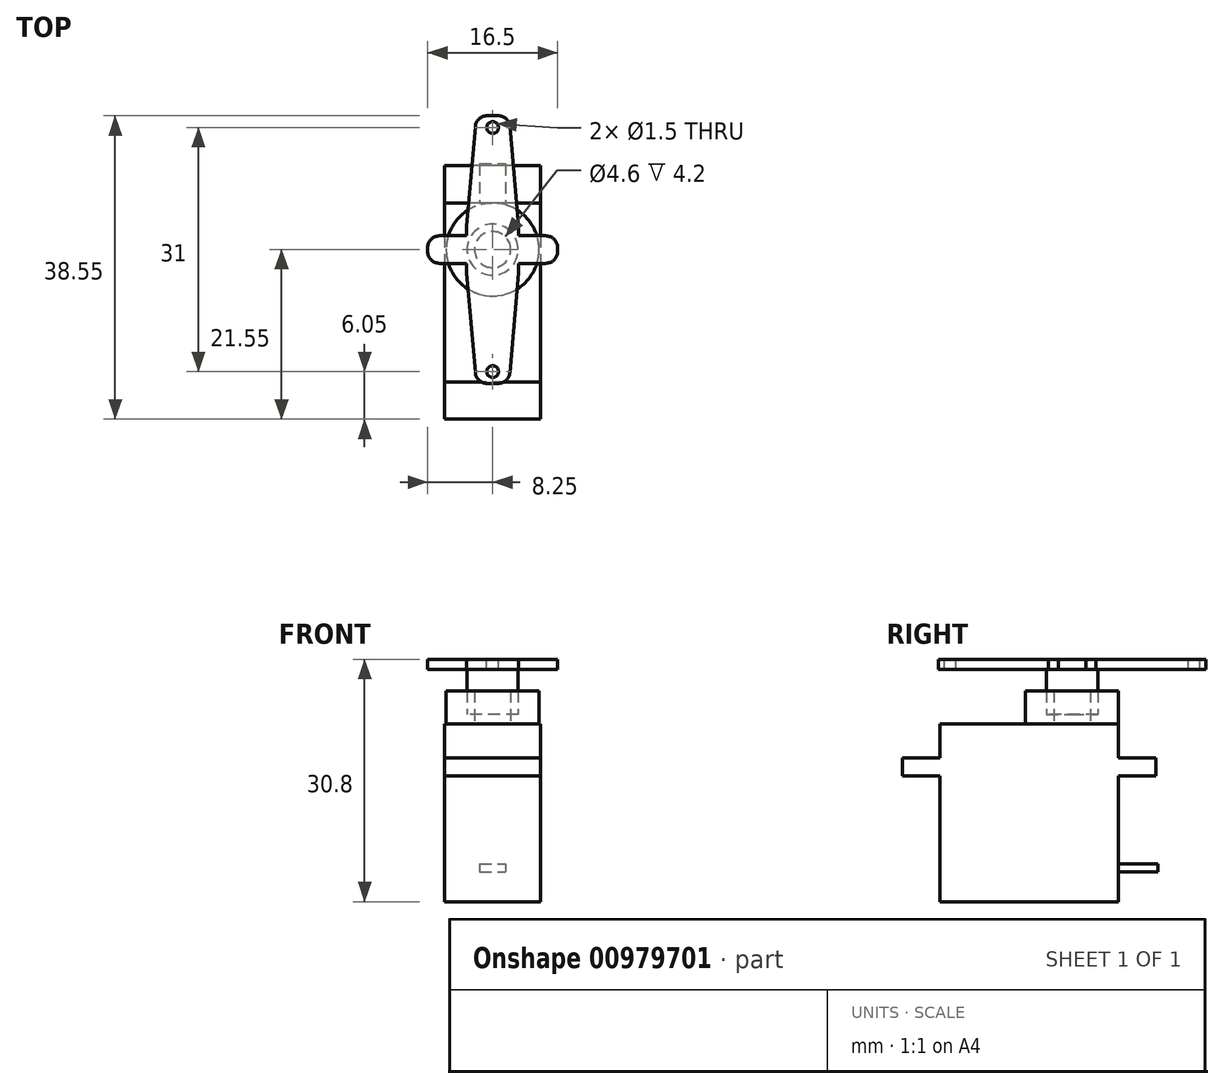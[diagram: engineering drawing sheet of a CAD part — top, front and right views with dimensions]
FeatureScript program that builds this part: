
annotation { "Feature Type Name" : "Feature", "Feature Type Description" : "" }
export const myFeature = defineFeature(function(context is Context, id is Id, definition is map)
    precondition{}
    {
        {
            var Q0;
            Q0=qCreatedBy(makeId("Top.planeOp"),FACE);
            var sketch = newSketch(context, id + "F0", { "sketchPlane" : qUnion([Q0])});
            skLineSegment(sketch, "E0.bottom", {"start": v(6.1, 11.35) * mm, "end": v(-6.1, 11.35) * mm});
            skLineSegment(sketch, "E0.top", {"start": v(6.1, -11.35) * mm, "end": v(-6.1, -11.35) * mm});
            skLineSegment(sketch, "E0.left", {"start": v(6.1, 11.35) * mm, "end": v(6.1, -11.35) * mm});
            skLineSegment(sketch, "E0.right", {"start": v(-6.1, 11.35) * mm, "end": v(-6.1, -11.35) * mm});
            skPoint(sketch, "E0.middle", {"position": v(0, 0) * mm});
            skSolve(sketch);
        }
        {
            var Q0;
            Q0=makeQuery(id+"F0.imprint","IMPRINT",FACE,{"disambiguationData":[TD([[makeQuery(id+"F0.imprint","IMPRINT",EDGE,{"derivedFrom":sQuery(id+"F0.wireOp",EDGE,"E0.bottom")}),1.0]])]});
            extrude(context, id + "F1", {"entities" : qUnion([Q0]), "depth" : 16 * mm, "offsetDistance" : 25 * mm});
        }
        {
            var Q0;
            Q0=makeQuery(id+"F1.opExtrude","CAP_FACE",FACE,{"disambiguationData":[OSD([sQuery(id+"F0.wireOp",EDGE,"E0.bottom"),sQuery(id+"F0.wireOp",EDGE,"E0.top"),sQuery(id+"F0.wireOp",EDGE,"E0.left"),sQuery(id+"F0.wireOp",EDGE,"E0.right")])],"isStart":false});
            var sketch = newSketch(context, id + "F2", { "sketchPlane" : qUnion([Q0])});
            skLineSegment(sketch, "E1.bottom", {"start": v(6.1, 16.1) * mm, "end": v(-6.1, 16.1) * mm});
            skLineSegment(sketch, "E1.top", {"start": v(6.1, -16.1) * mm, "end": v(-6.1, -16.1) * mm});
            skLineSegment(sketch, "E1.left", {"start": v(6.1, 16.1) * mm, "end": v(6.1, -16.1) * mm});
            skLineSegment(sketch, "E1.right", {"start": v(-6.1, 16.1) * mm, "end": v(-6.1, -16.1) * mm});
            skPoint(sketch, "E1.middle", {"position": v(0, 0) * mm});
            skSolve(sketch);
        }
        {
            var Q0;
            Q0 = qSketchRegion(id + "F2", true);
            extrude(context, id + "F3", {"entities" : qUnion([Q0]), "operationType" : NewBodyOperationType.ADD, "depth" : 2.3 * mm, "offsetDistance" : 25 * mm});
        }
        {
            var Q0;
            Q0=makeQuery(id+"F3.opExtrude","CAP_FACE",FACE,{"disambiguationData":[OSD([sQuery(id+"F2.wireOp",EDGE,"E1.bottom"),sQuery(id+"F2.wireOp",EDGE,"E1.top"),sQuery(id+"F2.wireOp",EDGE,"E1.left"),sQuery(id+"F2.wireOp",EDGE,"E1.right")])],"isStart":false});
            var sketch = newSketch(context, id + "F4", { "sketchPlane" : qUnion([Q0])});
            skLineSegment(sketch, "E2.bottom", {"start": v(6.1, 11.35) * mm, "end": v(-6.1, 11.35) * mm});
            skLineSegment(sketch, "E2.top", {"start": v(6.1, -11.35) * mm, "end": v(-6.1, -11.35) * mm});
            skLineSegment(sketch, "E2.left", {"start": v(6.1, 11.35) * mm, "end": v(6.1, -11.35) * mm});
            skLineSegment(sketch, "E2.right", {"start": v(-6.1, 11.35) * mm, "end": v(-6.1, -11.35) * mm});
            skPoint(sketch, "E2.middle", {"position": v(0, 0) * mm});
            skSolve(sketch);
        }
        {
            var Q0;
            Q0 = qSketchRegion(id + "F4", true);
            extrude(context, id + "F5", {"entities" : qUnion([Q0]), "operationType" : NewBodyOperationType.ADD, "depth" : 4.3 * mm, "offsetDistance" : 25 * mm});
        }
        {
            var Q0;
            Q0=makeQuery(id+"F5.opExtrude","CAP_FACE",FACE,{"disambiguationData":[OSD([sQuery(id+"F4.wireOp",EDGE,"E2.bottom"),sQuery(id+"F4.wireOp",EDGE,"E2.top"),sQuery(id+"F4.wireOp",EDGE,"E2.left"),sQuery(id+"F4.wireOp",EDGE,"E2.right")])],"isStart":false});
            var sketch = newSketch(context, id + "F6", { "sketchPlane" : qUnion([Q0])});
            skCircle(sketch, "E3", {"center": v(0, 5.45) * mm, "radius": 5.9 * mm});
            skCircle(sketch, "E4", {"center": v(0, 5.45) * mm, "radius": 2.3 * mm});
            skSolve(sketch);
        }
        {
            var Q0;
            Q0 = qSketchRegion(id + "F6", true);
            extrude(context, id + "F7", {"entities" : qUnion([Q0]), "operationType" : NewBodyOperationType.ADD, "depth" : 4.2 * mm, "offsetDistance" : 25 * mm});
        }
        {
            var Q0;
            Q0=makeQuery(id+"F1.opExtrude","SWEPT_FACE",FACE,{"disambiguationData":[OSD([sQuery(id+"F0.wireOp",EDGE,"E0.bottom")])]});
            var sketch = newSketch(context, id + "F8", { "sketchPlane" : qUnion([Q0])});
            skLineSegment(sketch, "E5.bottom", {"start": v(1.65, 4.8) * mm, "end": v(-1.65, 4.8) * mm});
            skLineSegment(sketch, "E5.top", {"start": v(1.65, 3.8) * mm, "end": v(-1.65, 3.8) * mm});
            skLineSegment(sketch, "E5.left", {"start": v(1.65, 4.8) * mm, "end": v(1.65, 3.8) * mm});
            skLineSegment(sketch, "E5.right", {"start": v(-1.65, 4.8) * mm, "end": v(-1.65, 3.8) * mm});
            skPoint(sketch, "E5.middle", {"position": v(0, 4.3) * mm});
            skSolve(sketch);
        }
        {
            var Q0;
            Q0 = qSketchRegion(id + "F8", true);
            extrude(context, id + "F9", {"entities" : qUnion([Q0]), "operationType" : NewBodyOperationType.ADD, "depth" : 5 * mm, "offsetDistance" : 25 * mm});
        }
        {
            var Q0;
            Q0=makeQuery(id+"F7.opExtrude","CAP_FACE",FACE,{"disambiguationData":[OSD([sQuery(id+"F6.wireOp",EDGE,"E3"),sQuery(id+"F6.wireOp",EDGE,"E4")])],"isStart":false});
            var sketch = newSketch(context, id + "F10", { "sketchPlane" : qUnion([Q0])});
            skCircle(sketch, "E6", {"center": v(0, 5.45) * mm, "radius": 3.25 * mm});
            skSolve(sketch);
        }
        {
            var Q0;
            Q0 = qSketchRegion(id + "F10", true);
            extrude(context, id + "F11", {"entities" : qUnion([Q0]), "depth" : 4 * mm, "offsetDistance" : 25 * mm, "hasSecondDirection" : true, "secondDirectionOppositeDirection" : true, "secondDirectionDepth" : 3 * mm});
        }
        {
            var Q0;
            Q0=makeQuery(id+"F11.opExtrude","CAP_FACE",FACE,{"disambiguationData":[OSD([sQuery(id+"F10.wireOp",EDGE,"E6")])],"isStart":false});
            var sketch = newSketch(context, id + "F12", { "sketchPlane" : qUnion([Q0])});
            skLineSegment(sketch, "E7.bottom", {"start": v(3.3, 22.45) * mm, "end": v(-3.3, 22.45) * mm});
            skLineSegment(sketch, "E7.top", {"start": v(3.3, -11.55) * mm, "end": v(-3.3, -11.55) * mm});
            skLineSegment(sketch, "E7.left", {"start": v(3.3, 22.45) * mm, "end": v(3.3, 7.2) * mm});
            skLineSegment(sketch, "E7.right", {"start": v(-3.3, 22.45) * mm, "end": v(-3.3, 7.2) * mm});
            skPoint(sketch, "E7.middle", {"position": v(0, 5.45) * mm});
            skLineSegment(sketch, "E8.bottom", {"start": v(8.25, 7.2) * mm, "end": v(3.3, 7.2) * mm});
            skLineSegment(sketch, "E8.top", {"start": v(8.25, 3.7) * mm, "end": v(3.3, 3.7) * mm});
            skLineSegment(sketch, "E8.left", {"start": v(8.25, 7.2) * mm, "end": v(8.25, 3.7) * mm});
            skLineSegment(sketch, "E8.right", {"start": v(-8.25, 7.2) * mm, "end": v(-8.25, 3.7) * mm});
            skLineSegment(sketch, "E9.trimOffspring", {"start": v(-3.3, 7.2) * mm, "end": v(-8.25, 7.2) * mm});
            skLineSegment(sketch, "E10.trimOffspring", {"start": v(-3.3, 3.7) * mm, "end": v(-3.3, -11.55) * mm});
            skLineSegment(sketch, "E11.trimOffspring", {"start": v(-3.3, 3.7) * mm, "end": v(-8.25, 3.7) * mm});
            skLineSegment(sketch, "E12.trimOffspring", {"start": v(3.3, 3.7) * mm, "end": v(3.3, -11.55) * mm});
            skCircle(sketch, "E13", {"center": v(0, 20.95) * mm, "radius": 0.75 * mm});
            skPoint(sketch, "E13.centerSnap0", {"position": v(0, 22.45) * mm});
            skCircle(sketch, "E14", {"center": v(0, -10.05) * mm, "radius": 0.75 * mm});
            skSolve(sketch);
        }
        {
            var Q0;
            Q0 = qSketchRegion(id + "F12", true);
            extrude(context, id + "F13", {"entities" : qUnion([Q0]), "operationType" : NewBodyOperationType.ADD, "oppositeDirection" : true, "depth" : 1.3 * mm, "offsetDistance" : 25 * mm});
        }
        {
            var Q0;
            Q0=makeQuery(id+"F13.opExtrude","SWEPT_EDGE",EDGE,{"disambiguationData":[OSD([sQuery(id+"F12.wireOp",EDGE,"E7.top"),sQuery(id+"F12.wireOp",EDGE,"E10.trimOffspring")])]});
            var Q1;
            Q1=makeQuery(id+"F13.opExtrude","SWEPT_EDGE",EDGE,{"disambiguationData":[OSD([sQuery(id+"F12.wireOp",EDGE,"E7.top"),sQuery(id+"F12.wireOp",EDGE,"E12.trimOffspring")])]});
            var Q2;
            Q2=makeQuery(id+"F13.opExtrude","SWEPT_EDGE",EDGE,{"disambiguationData":[OSD([sQuery(id+"F12.wireOp",EDGE,"E7.bottom"),sQuery(id+"F12.wireOp",EDGE,"E7.left")])]});
            chamfer(context, id + "F14", {"entities" : qUnion([Q0, Q1, Q2]), "chamferType" : ChamferType.OFFSET_ANGLE, "width" : 14 * mm, "oppositeDirection" : false, "angle" : 5 * degree, "tangentPropagation" : true});
        }
        {
            var Q0;
            Q0=makeQuery(id+"F13.opExtrude","SWEPT_EDGE",EDGE,{"disambiguationData":[OSD([sQuery(id+"F12.wireOp",EDGE,"E7.bottom"),sQuery(id+"F12.wireOp",EDGE,"E7.right")])]});
            chamfer(context, id + "F15", {"entities" : qUnion([Q0]), "chamferType" : ChamferType.OFFSET_ANGLE, "width" : 14 * mm, "oppositeDirection" : true, "angle" : 5 * degree, "tangentPropagation" : true});
        }
        {
            var Q0;
            {var subQ0=sQuery(id+"F12.wireOp",EDGE,"E7.bottom");Q0=makeQuery(id+"F15.opChamfer","BLEND_EDGE",EDGE,{"blendedFrom":[makeQuery(id+"F13.opExtrude","SWEPT_EDGE",EDGE,{"disambiguationData":[OSD([subQ0,sQuery(id+"F12.wireOp",EDGE,"E7.right")])]}),makeQuery(id+"F13.opExtrude","SWEPT_FACE",FACE,{"disambiguationData":[OSD([subQ0])]})],"blendedInto":[makeQuery(id+"F13.opExtrude","SWEPT_FACE",FACE,{"disambiguationData":[OSD([subQ0])]})]});}
            var Q1;
            {var subQ0=sQuery(id+"F12.wireOp",EDGE,"E7.bottom");Q1=makeQuery(id+"F14.opChamfer","BLEND_EDGE",EDGE,{"blendedFrom":[makeQuery(id+"F13.opExtrude","SWEPT_EDGE",EDGE,{"disambiguationData":[OSD([subQ0,sQuery(id+"F12.wireOp",EDGE,"E7.left")])]}),makeQuery(id+"F13.opExtrude","SWEPT_FACE",FACE,{"disambiguationData":[OSD([subQ0])]})],"blendedInto":[makeQuery(id+"F13.opExtrude","SWEPT_FACE",FACE,{"disambiguationData":[OSD([subQ0])]})]});}
            var Q2;
            Q2=makeQuery(id+"F13.opExtrude","SWEPT_EDGE",EDGE,{"disambiguationData":[OSD([sQuery(id+"F12.wireOp",EDGE,"E8.right"),sQuery(id+"F12.wireOp",EDGE,"E9.trimOffspring")])]});
            var Q3;
            Q3=makeQuery(id+"F13.opExtrude","SWEPT_EDGE",EDGE,{"disambiguationData":[OSD([sQuery(id+"F12.wireOp",EDGE,"E8.right"),sQuery(id+"F12.wireOp",EDGE,"E11.trimOffspring")])]});
            var Q4;
            Q4=makeQuery(id+"F13.opExtrude","SWEPT_EDGE",EDGE,{"disambiguationData":[OSD([sQuery(id+"F12.wireOp",EDGE,"E8.bottom"),sQuery(id+"F12.wireOp",EDGE,"E8.left")])]});
            var Q5;
            Q5=makeQuery(id+"F13.opExtrude","SWEPT_EDGE",EDGE,{"disambiguationData":[OSD([sQuery(id+"F12.wireOp",EDGE,"E8.top"),sQuery(id+"F12.wireOp",EDGE,"E8.left")])]});
            var Q6;
            {var subQ0=sQuery(id+"F12.wireOp",EDGE,"E7.top");Q6=makeQuery(id+"F14.opChamfer","BLEND_EDGE",EDGE,{"blendedFrom":[makeQuery(id+"F13.opExtrude","SWEPT_EDGE",EDGE,{"disambiguationData":[OSD([subQ0,sQuery(id+"F12.wireOp",EDGE,"E12.trimOffspring")])]}),makeQuery(id+"F13.opExtrude","SWEPT_FACE",FACE,{"disambiguationData":[OSD([subQ0])]})],"blendedInto":[makeQuery(id+"F13.opExtrude","SWEPT_FACE",FACE,{"disambiguationData":[OSD([subQ0])]})]});}
            var Q7;
            {var subQ0=sQuery(id+"F12.wireOp",EDGE,"E7.top");Q7=makeQuery(id+"F14.opChamfer","BLEND_EDGE",EDGE,{"blendedFrom":[makeQuery(id+"F13.opExtrude","SWEPT_EDGE",EDGE,{"disambiguationData":[OSD([subQ0,sQuery(id+"F12.wireOp",EDGE,"E10.trimOffspring")])]}),makeQuery(id+"F13.opExtrude","SWEPT_FACE",FACE,{"disambiguationData":[OSD([subQ0])]})],"blendedInto":[makeQuery(id+"F13.opExtrude","SWEPT_FACE",FACE,{"disambiguationData":[OSD([subQ0])]})]});}
            fillet(context, id + "F16", {"entities" : qUnion([Q0, Q1, Q2, Q3, Q4, Q5, Q6, Q7]), "tangentPropagation" : true, "radius" : 1.5 * mm, "defaultsChanged" : true, "vertexSettings" : [], "allowEdgeOverflow" : false});
        }
    });
